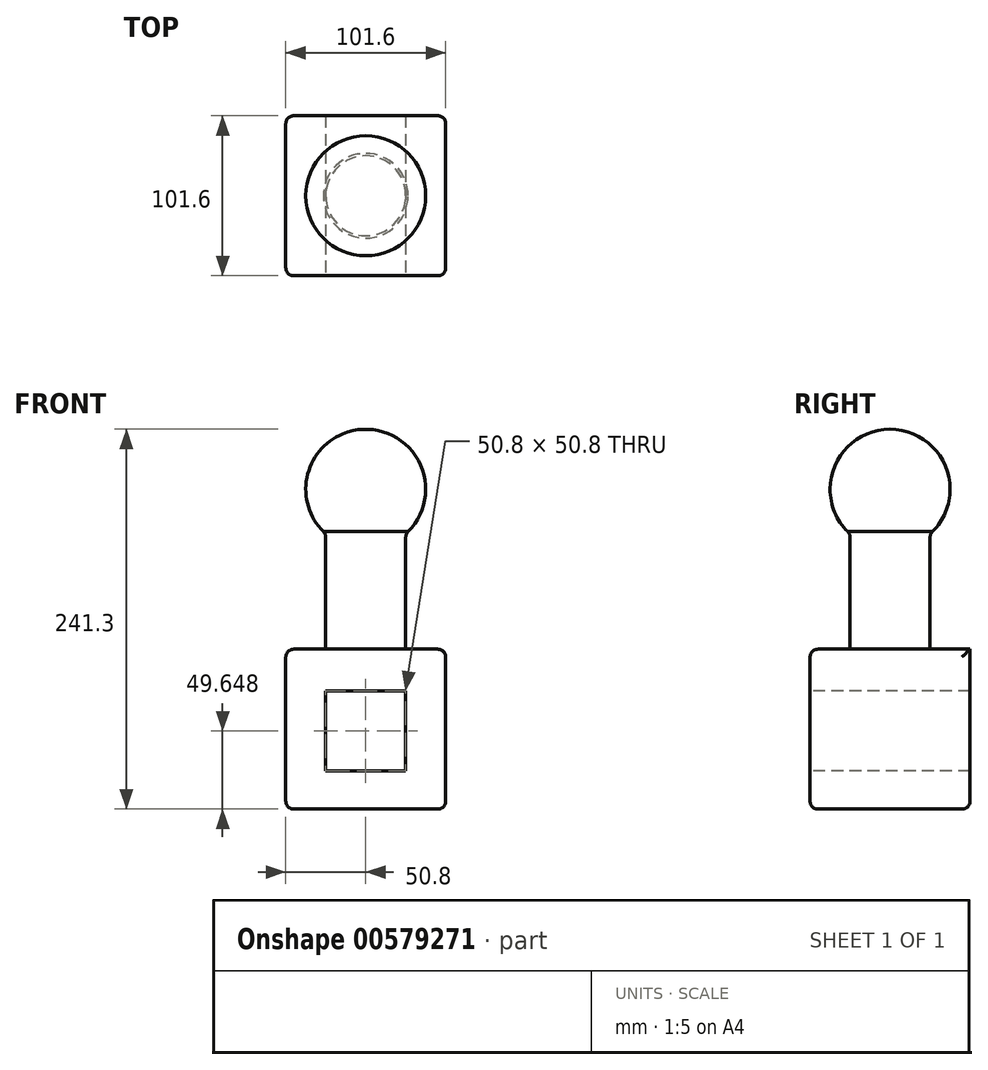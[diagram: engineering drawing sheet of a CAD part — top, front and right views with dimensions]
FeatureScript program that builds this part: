
annotation { "Feature Type Name" : "Feature", "Feature Type Description" : "" }
export const myFeature = defineFeature(function(context is Context, id is Id, definition is map)
    precondition{}
    {
        {
            var Q0;
            Q0=qCreatedBy(makeId("Top.planeOp"),FACE);
            var sketch = newSketch(context, id + "F0", { "sketchPlane" : qUnion([Q0])});
            skLineSegment(sketch, "E0.bottom", {"start": v(50.8, -50.8) * mm, "end": v(-50.8, -50.8) * mm});
            skLineSegment(sketch, "E0.top", {"start": v(50.8, 50.8) * mm, "end": v(-50.8, 50.8) * mm});
            skLineSegment(sketch, "E0.left", {"start": v(50.8, -50.8) * mm, "end": v(50.8, 50.8) * mm});
            skLineSegment(sketch, "E0.right", {"start": v(-50.8, -50.8) * mm, "end": v(-50.8, 50.8) * mm});
            skPoint(sketch, "E0.middle", {"position": v(0, 0) * mm});
            skSolve(sketch);
        }
        {
            var Q0;
            Q0 = qSketchRegion(id + "F0", true);
            extrude(context, id + "F1", {"entities" : qUnion([Q0]), "depth" : 101.6 * mm, "offsetDistance" : 25.4 * mm});
        }
        {
            var Q0;
            Q0=makeQuery(id+"F1.opExtrude","CAP_FACE",FACE,{"disambiguationData":[OSD([sQuery(id+"F0.wireOp",EDGE,"E0.bottom"),sQuery(id+"F0.wireOp",EDGE,"E0.top"),sQuery(id+"F0.wireOp",EDGE,"E0.left"),sQuery(id+"F0.wireOp",EDGE,"E0.right")])],"isStart":false});
            var sketch = newSketch(context, id + "F2", { "sketchPlane" : qUnion([Q0])});
            skCircle(sketch, "E1", {"center": v(0, 0) * mm, "radius": 25.4 * mm});
            skSolve(sketch);
        }
        {
            var Q0;
            Q0=makeQuery(id+"F2.imprint","IMPRINT",FACE,{"disambiguationData":[TD([[makeQuery(id+"F2.imprint","IMPRINT",EDGE,{"derivedFrom":sQuery(id+"F2.wireOp",EDGE,"E1")}),1.0]])]});
            extrude(context, id + "F3", {"entities" : qUnion([Q0]), "operationType" : NewBodyOperationType.ADD, "depth" : 101.6 * mm, "offsetDistance" : 25.4 * mm});
        }
        {
            var Q0;
            Q0=makeQuery(id+"F3.opExtrude","CAP_FACE",FACE,{"disambiguationData":[OSD([sQuery(id+"F2.wireOp",EDGE,"E1")])],"isStart":false});
            var sketch = newSketch(context, id + "F4", { "sketchPlane" : qUnion([Q0])});
            skArc(sketch, "E2", {"start": v(0, -38.1) * mm, "mid": v(38.1, 0) * mm, "end": v(0, 38.1) * mm});
            skLineSegment(sketch, "E3", {"start": v(0, 38.1) * mm, "end": v(0, -38.1) * mm});
            skSolve(sketch);
        }
        {
            var Q0;
            Q0 = qSketchRegion(id + "F4", true);
            var Q1;
            Q1=sQuery(id+"F4.wireOp",EDGE,"E3");
            revolve(context, id + "F5", {"operationType" : NewBodyOperationType.ADD, "entities" : qUnion([Q0]), "axis" : qUnion([Q1]), "revolveType" : RevolveType.FULL});
        }
        {
            var Q0;
            Q0=makeQuery(id+"F1.opExtrude","SWEPT_FACE",FACE,{"disambiguationData":[OSD([sQuery(id+"F0.wireOp",EDGE,"E0.bottom")])]});
            var sketch = newSketch(context, id + "F6", { "sketchPlane" : qUnion([Q0])});
            skLineSegment(sketch, "E4.bottom", {"start": v(-25.4, 75.05) * mm, "end": v(25.4, 75.05) * mm});
            skLineSegment(sketch, "E4.top", {"start": v(-25.4, 24.25) * mm, "end": v(25.4, 24.25) * mm});
            skLineSegment(sketch, "E4.left", {"start": v(-25.4, 75.05) * mm, "end": v(-25.4, 24.25) * mm});
            skLineSegment(sketch, "E4.right", {"start": v(25.4, 75.05) * mm, "end": v(25.4, 24.25) * mm});
            skPoint(sketch, "E4.middle", {"position": v(0, 49.65) * mm});
            skSolve(sketch);
        }
        {
            var Q0;
            Q0=makeQuery(id+"F6.imprint","IMPRINT",FACE,{"disambiguationData":[TD([[makeQuery(id+"F6.imprint","IMPRINT",EDGE,{"derivedFrom":sQuery(id+"F6.wireOp",EDGE,"E4.bottom")}),-1.0]])]});
            extrude(context, id + "F7", {"entities" : qUnion([Q0]), "operationType" : NewBodyOperationType.REMOVE, "oppositeDirection" : true, "depth" : 101.6 * mm, "offsetDistance" : 25.4 * mm});
        }
        {
            var Q0;
            Q0=makeQuery(id+"F1.opExtrude","CAP_EDGE",EDGE,{"disambiguationData":[OSD([sQuery(id+"F0.wireOp",EDGE,"E0.bottom")])],"isStart":false});
            var Q1;
            Q1=makeQuery(id+"F1.opExtrude","CAP_EDGE",EDGE,{"disambiguationData":[OSD([sQuery(id+"F0.wireOp",EDGE,"E0.left")])],"isStart":false});
            var Q2;
            Q2=makeQuery(id+"F1.opExtrude","CAP_EDGE",EDGE,{"disambiguationData":[OSD([sQuery(id+"F0.wireOp",EDGE,"E0.left")])],"isStart":true});
            var Q3;
            Q3=makeQuery(id+"F1.opExtrude","SWEPT_EDGE",EDGE,{"disambiguationData":[OSD([sQuery(id+"F0.wireOp",EDGE,"E0.bottom"),sQuery(id+"F0.wireOp",EDGE,"E0.left")])]});
            var Q4;
            Q4=makeQuery(id+"F1.opExtrude","CAP_EDGE",EDGE,{"disambiguationData":[OSD([sQuery(id+"F0.wireOp",EDGE,"E0.bottom")])],"isStart":true});
            var Q5;
            Q5=makeQuery(id+"F1.opExtrude","SWEPT_EDGE",EDGE,{"disambiguationData":[OSD([sQuery(id+"F0.wireOp",EDGE,"E0.bottom"),sQuery(id+"F0.wireOp",EDGE,"E0.right")])]});
            var Q6;
            Q6=makeQuery(id+"F1.opExtrude","SWEPT_EDGE",EDGE,{"disambiguationData":[OSD([sQuery(id+"F0.wireOp",EDGE,"E0.top"),sQuery(id+"F0.wireOp",EDGE,"E0.left")])]});
            var Q7;
            Q7=makeQuery(id+"F1.opExtrude","CAP_EDGE",EDGE,{"disambiguationData":[OSD([sQuery(id+"F0.wireOp",EDGE,"E0.top")])],"isStart":true});
            var Q8;
            Q8=makeQuery(id+"F1.opExtrude","CAP_EDGE",EDGE,{"disambiguationData":[OSD([sQuery(id+"F0.wireOp",EDGE,"E0.right")])],"isStart":true});
            var Q9;
            Q9=makeQuery(id+"F1.opExtrude","SWEPT_EDGE",EDGE,{"disambiguationData":[OSD([sQuery(id+"F0.wireOp",EDGE,"E0.top"),sQuery(id+"F0.wireOp",EDGE,"E0.right")])]});
            var Q10;
            Q10=makeQuery(id+"F1.opExtrude","CAP_EDGE",EDGE,{"disambiguationData":[OSD([sQuery(id+"F0.wireOp",EDGE,"E0.right")])],"isStart":false});
            var Q11;
            Q11=makeQuery(id+"F3.opExtrude","CAP_EDGE",EDGE,{"disambiguationData":[OSD([sQuery(id+"F2.wireOp",EDGE,"E1")])],"isStart":true});
            var Q12;
            Q12=makeQuery(id+"F5.boolean.opBoolean","INTERSECT",EDGE,{"derivedFrom":[makeQuery(id+"F3.opExtrude","SWEPT_FACE",FACE,{"disambiguationData":[OSD([sQuery(id+"F2.wireOp",EDGE,"E1")])]}),makeQuery(id+"F5.opRevolve","SWEPT_FACE",FACE,{"disambiguationData":[OSD([sQuery(id+"F4.wireOp",EDGE,"E2")])]})]});
            fillet(context, id + "F8", {"entities" : qUnion([Q0, Q1, Q2, Q3, Q4, Q5, Q6, Q7, Q8, Q9, Q10, Q11, Q12]), "radius" : 5.08 * mm, "tangentPropagation" : true, "allowEdgeOverflow" : false});
        }
    });
